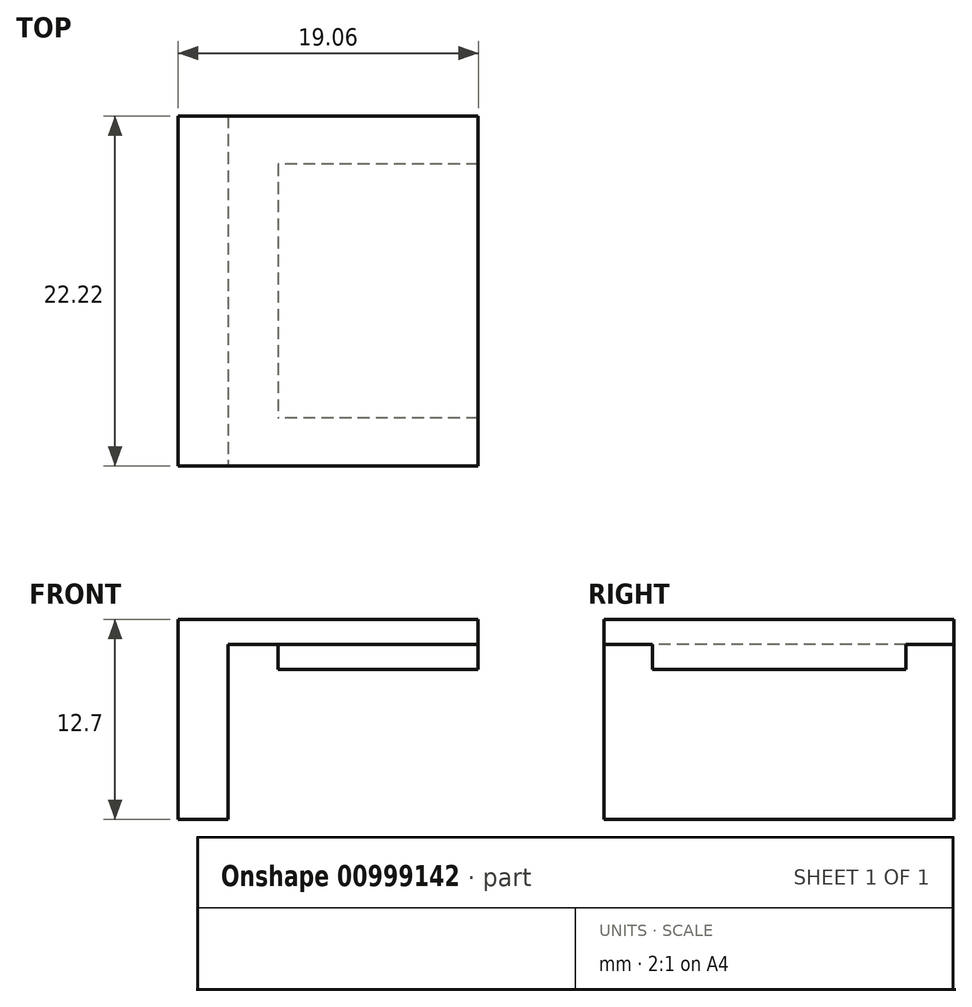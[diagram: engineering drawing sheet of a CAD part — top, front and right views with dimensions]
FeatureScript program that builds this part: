
annotation { "Feature Type Name" : "Feature", "Feature Type Description" : "" }
export const myFeature = defineFeature(function(context is Context, id is Id, definition is map)
    precondition{}
    {
        {
            var Q0;
            Q0=qCreatedBy(makeId("Top.planeOp"),FACE);
            var sketch = newSketch(context, id + "F0", { "sketchPlane" : qUnion([Q0])});
            skLineSegment(sketch, "E0.bottom", {"start": v(9.53, 11.11) * mm, "end": v(-9.52, 11.11) * mm});
            skLineSegment(sketch, "E0.top", {"start": v(9.52, -11.11) * mm, "end": v(-9.53, -11.11) * mm});
            skLineSegment(sketch, "E0.left", {"start": v(9.53, 11.11) * mm, "end": v(9.52, -11.11) * mm});
            skLineSegment(sketch, "E0.right", {"start": v(-9.52, 11.11) * mm, "end": v(-9.53, -11.11) * mm});
            skPoint(sketch, "E0.middle", {"position": v(0, 0) * mm});
            skLineSegment(sketch, "E1.bottom", {"start": v(9.53, 11.11) * mm, "end": v(-3.18, 11.11) * mm});
            skLineSegment(sketch, "E1.top", {"start": v(9.53, -11.11) * mm, "end": v(-3.17, -11.11) * mm});
            skLineSegment(sketch, "E1.left", {"start": v(9.53, 11.11) * mm, "end": v(9.53, -11.11) * mm});
            skLineSegment(sketch, "E1.right", {"start": v(-3.18, 11.11) * mm, "end": v(-3.17, -11.11) * mm});
            skLineSegment(sketch, "E2.top", {"start": v(9.53, 8.06) * mm, "end": v(-3.18, 8.06) * mm});
            skLineSegment(sketch, "E2.left", {"start": v(9.53, 11.11) * mm, "end": v(9.53, 8.06) * mm});
            skLineSegment(sketch, "E2.right", {"start": v(-3.18, 11.11) * mm, "end": v(-3.18, 8.06) * mm});
            skLineSegment(sketch, "E3.bottom", {"start": v(9.52, -11.11) * mm, "end": v(-3.17, -11.11) * mm});
            skLineSegment(sketch, "E3.top", {"start": v(9.52, -8.06) * mm, "end": v(-3.17, -8.06) * mm});
            skLineSegment(sketch, "E3.left", {"start": v(9.52, -11.11) * mm, "end": v(9.52, -8.06) * mm});
            skLineSegment(sketch, "E3.right", {"start": v(-3.17, -11.11) * mm, "end": v(-3.17, -8.06) * mm});
            skLineSegment(sketch, "E4.bottom", {"start": v(-9.52, 11.11) * mm, "end": v(-6.35, 11.11) * mm});
            skLineSegment(sketch, "E4.top", {"start": v(-9.52, -11.11) * mm, "end": v(-6.35, -11.11) * mm});
            skLineSegment(sketch, "E4.left", {"start": v(-9.52, 11.11) * mm, "end": v(-9.52, -11.11) * mm});
            skLineSegment(sketch, "E4.right", {"start": v(-6.35, 11.11) * mm, "end": v(-6.35, -11.11) * mm});
            skSolve(sketch);
        }
        {
            var Q0;
            {var subQ5=sQuery(id+"F0.wireOp",EDGE,"E4.right");Q0=makeQuery(id+"F0.imprint","IMPRINT",FACE,{"disambiguationData":[TD([[makeQuery(id+"F0.imprint","IMPRINT",EDGE,{"derivedFrom":subQ5}),1.0]])]});}
            var Q1;
            {var subQ5=sQuery(id+"F0.wireOp",EDGE,"E3.top");Q1=makeQuery(id+"F0.imprint","IMPRINT",FACE,{"disambiguationData":[TD([[makeQuery(id+"F0.imprint","IMPRINT",EDGE,{"derivedFrom":subQ5}),1.0]])]});}
            var Q2;
            {var subQ5=sQuery(id+"F0.wireOp",EDGE,"E2.top");Q2=makeQuery(id+"F0.imprint","IMPRINT",FACE,{"disambiguationData":[TD([[makeQuery(id+"F0.imprint","IMPRINT",EDGE,{"derivedFrom":subQ5}),-1.0]])]});}
            extrude(context, id + "F1", {"entities" : qUnion([Q0, Q1, Q2]), "oppositeDirection" : true, "depth" : 1.59 * mm, "offsetDistance" : 25.4 * mm});
        }
        {
            var Q0;
            {var subQ2=sQuery(id+"F0.wireOp",EDGE,"E0.right");Q0=makeQuery(id+"F0.imprint","IMPRINT",FACE,{"disambiguationData":[TD([[makeQuery(id+"F0.imprint","IMPRINT",EDGE,{"derivedFrom":subQ2}),1.0]])]});}
            extrude(context, id + "F2", {"entities" : qUnion([Q0]), "operationType" : NewBodyOperationType.ADD, "oppositeDirection" : true, "depth" : 12.7 * mm, "offsetDistance" : 25.4 * mm});
        }
        {
            var Q0;
            {var subQ0=sQuery(id+"F0.wireOp",EDGE,"E2.top");Q0=makeQuery(id+"F0.imprint","IMPRINT",FACE,{"disambiguationData":[TD([[makeQuery(id+"F0.imprint","IMPRINT",EDGE,{"derivedFrom":subQ0}),1.0]])]});}
            extrude(context, id + "F3", {"entities" : qUnion([Q0]), "operationType" : NewBodyOperationType.ADD, "oppositeDirection" : true, "depth" : 3.17 * mm, "offsetDistance" : 25.4 * mm});
        }
    });
